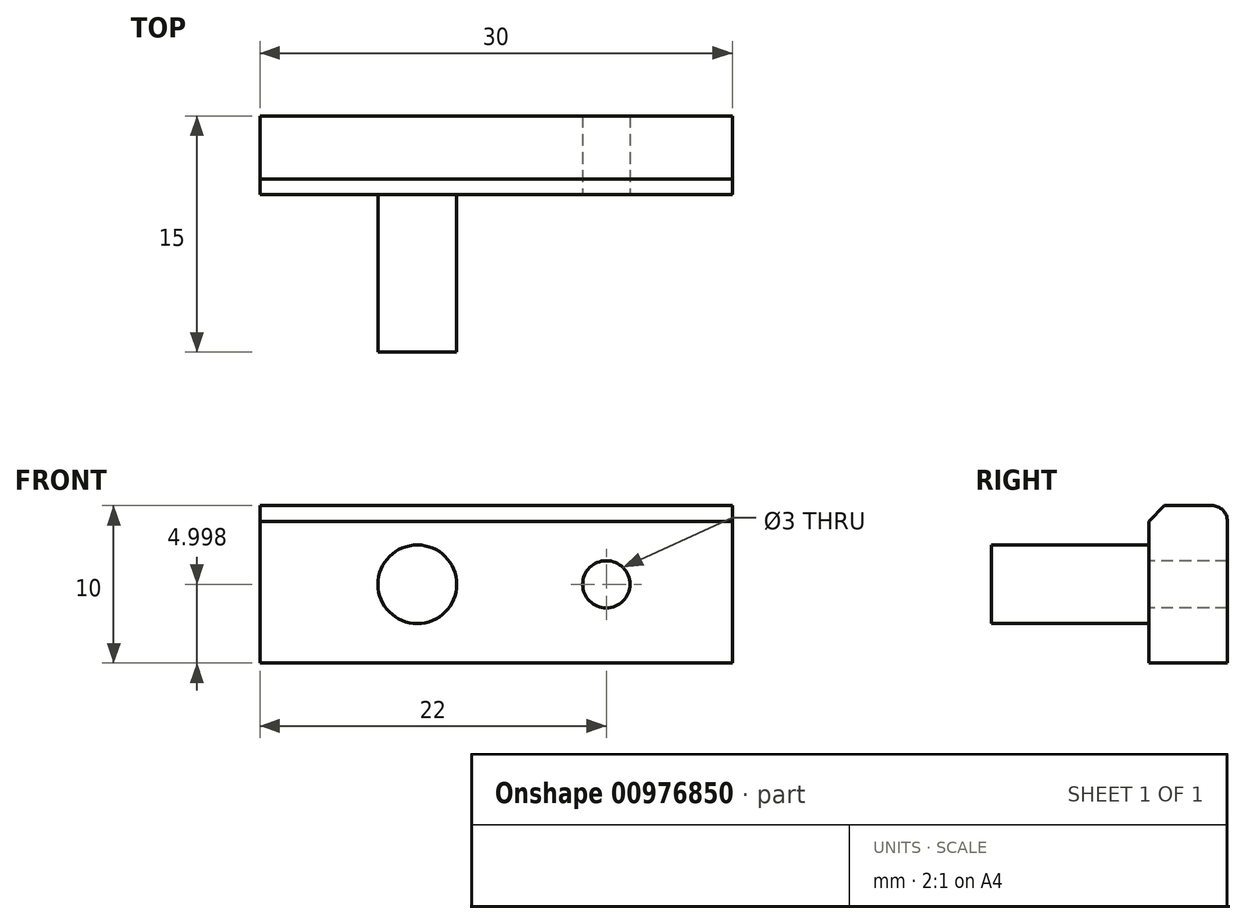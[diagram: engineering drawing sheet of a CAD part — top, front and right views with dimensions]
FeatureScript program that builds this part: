
annotation { "Feature Type Name" : "Feature", "Feature Type Description" : "" }
export const myFeature = defineFeature(function(context is Context, id is Id, definition is map)
    precondition{}
    {
        {
            var Q0;
            Q0=qCreatedBy(makeId("Front.planeOp"),FACE);
            var sketch = newSketch(context, id + "F0", { "sketchPlane" : qUnion([Q0])});
            skLineSegment(sketch, "E0.bottom", {"start": v(0, 15.8) * mm, "end": v(30, 15.8) * mm});
            skLineSegment(sketch, "E0.top", {"start": v(0, 5.8) * mm, "end": v(30, 5.8) * mm});
            skLineSegment(sketch, "E0.left", {"start": v(0, 15.8) * mm, "end": v(0, 5.8) * mm});
            skLineSegment(sketch, "E0.right", {"start": v(30, 15.8) * mm, "end": v(30, 5.8) * mm});
            skSolve(sketch);
        }
        {
            var Q0;
            Q0 = qSketchRegion(id + "F0", true);
            var Q1;
            Q1=makeQuery(id+"F0.imprint","IMPRINT",FACE,{"disambiguationData":[TD([[makeQuery(id+"F0.imprint","IMPRINT",EDGE,{"derivedFrom":sQuery(id+"F0.wireOp",EDGE,"p0bg2yil-Z3VG-oHN7-xxF3-zuvsosKDiuty")}),1.0]])]});
            extrude(context, id + "F1", {"entities" : qUnion([Q0, Q1]), "depth" : 5 * mm, "offsetDistance" : 25 * mm});
        }
        {
            var Q0;
            Q0=makeQuery(id+"F1.opExtrude","CAP_FACE",FACE,{"disambiguationData":[OSD([sQuery(id+"F0.wireOp",EDGE,"E0.bottom"),sQuery(id+"F0.wireOp",EDGE,"E0.top"),sQuery(id+"F0.wireOp",EDGE,"E0.left"),sQuery(id+"F0.wireOp",EDGE,"E0.right")])],"isStart":false});
            var sketch = newSketch(context, id + "F2", { "sketchPlane" : qUnion([Q0])});
            skCircle(sketch, "E1", {"center": v(10, 10.8) * mm, "radius": 2.5 * mm});
            skCircle(sketch, "E2", {"center": v(20, 10.8) * mm, "radius": 1.5 * mm});
            skSolve(sketch);
        }
        {
            var Q0;
            Q0=makeQuery(id+"F2.imprint","IMPRINT",FACE,{"disambiguationData":[TD([[makeQuery(id+"F2.imprint","IMPRINT",EDGE,{"derivedFrom":sQuery(id+"F2.wireOp",EDGE,"E1")}),1.0]])]});
            extrude(context, id + "F3", {"entities" : qUnion([Q0]), "operationType" : NewBodyOperationType.ADD, "depth" : 10 * mm, "offsetDistance" : 25 * mm});
        }
        {
            var Q0;
            Q0=makeQuery(id+"F1.opExtrude","CAP_FACE",FACE,{"disambiguationData":[OSD([sQuery(id+"F0.wireOp",EDGE,"E0.bottom"),sQuery(id+"F0.wireOp",EDGE,"E0.top"),sQuery(id+"F0.wireOp",EDGE,"E0.left"),sQuery(id+"F0.wireOp",EDGE,"E0.right")])],"isStart":false});
            var sketch = newSketch(context, id + "F4", { "sketchPlane" : qUnion([Q0])});
            skCircle(sketch, "E3", {"center": v(22, 10.8) * mm, "radius": 1.5 * mm});
            skSolve(sketch);
        }
        {
            var Q0;
            Q0=makeQuery(id+"F4.imprint","IMPRINT",FACE,{"disambiguationData":[TD([[makeQuery(id+"F4.imprint","IMPRINT",EDGE,{"derivedFrom":sQuery(id+"F4.wireOp",EDGE,"E3")}),1.0]])]});
            var Q1;
            Q1=sQuery(id+"F4.wireOp",EDGE,"E3");
            extrude(context, id + "F5", {"entities" : qUnion([Q0]), "operationType" : NewBodyOperationType.REMOVE, "surfaceEntities" : qUnion([Q1]), "endBound" : BoundingType.THROUGH_ALL, "oppositeDirection" : true, "depth" : 25 * mm, "offsetDistance" : 25 * mm});
        }
        {
            var Q0;
            Q0=makeQuery(id+"F1.opExtrude","CAP_EDGE",EDGE,{"disambiguationData":[OSD([sQuery(id+"F0.wireOp",EDGE,"E0.bottom")])],"isStart":false});
            chamfer(context, id + "F6", {"entities" : qUnion([Q0]), "width" : 1 * mm, "tangentPropagation" : true});
        }
        {
            var Q0;
            Q0=makeQuery(id+"F1.opExtrude","CAP_EDGE",EDGE,{"disambiguationData":[OSD([sQuery(id+"F0.wireOp",EDGE,"E0.bottom")])],"isStart":true});
            fillet(context, id + "F7", {"entities" : qUnion([Q0]), "radius" : 1 * mm, "tangentPropagation" : true, "allowEdgeOverflow" : false});
        }
    });
